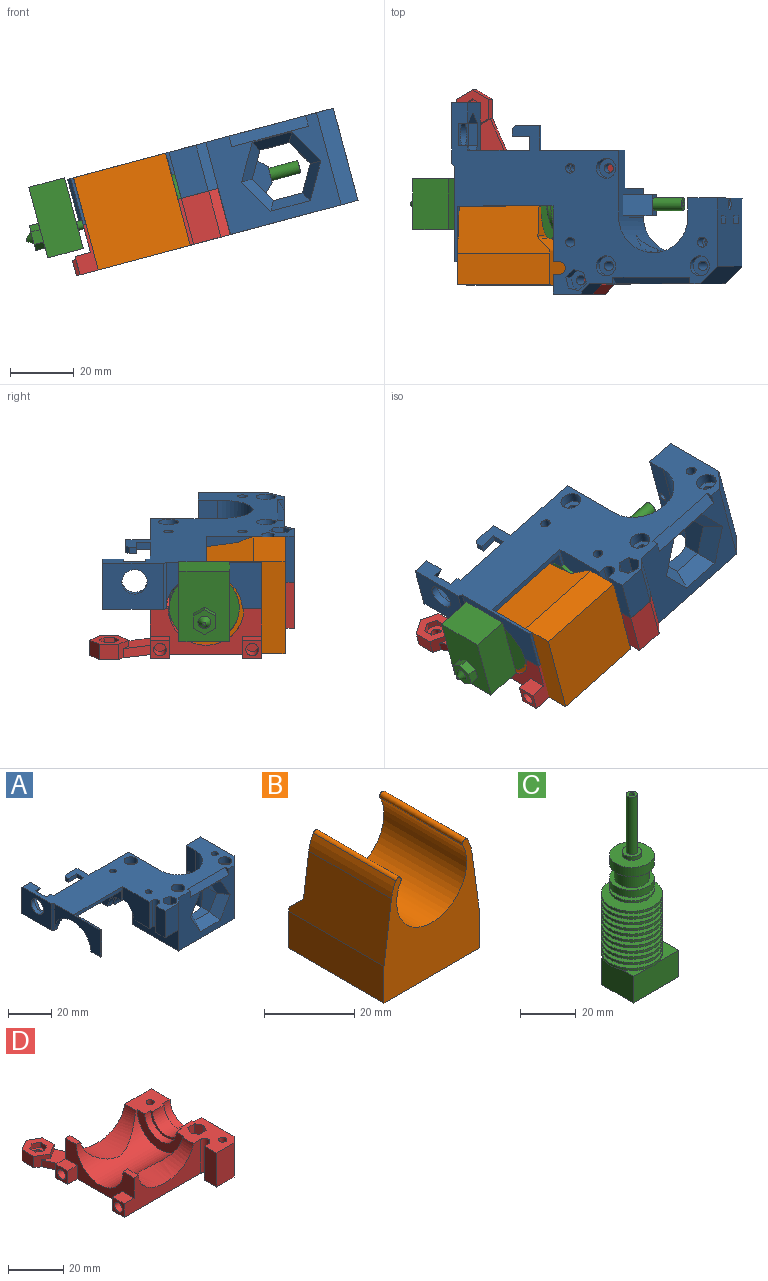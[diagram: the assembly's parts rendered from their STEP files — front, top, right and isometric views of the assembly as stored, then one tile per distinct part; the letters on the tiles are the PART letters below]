
ASSEMBLY  parts=4 mates=3
PART A: 169 faces, bbox 87.6x61.3x31.1 mm
  f0: plane 5.38x3mm, normal (-1,0,0), area 16.2mm2, adj f1,f165,f166,f168
  f1: plane 8.2x5.65mm, normal (0,1,0), area 34.3mm2, adj f0,f2,f5,f162,f163,f164,f165,f168
  f2: plane 8.9x3mm, normal (1,0,0), area 26.7mm2, adj f1,f3,f165,f168
  f3: plane 4x3mm, normal (0,1,0), area 12mm2, adj f2,f4,f165,f168
  f4: plane 3x2.63mm, normal (-1,0,0), area 7.9mm2, adj f3,f165,f166,f168
  f5: plane 8.2x2.5mm, normal (0,0,-1), area 20.5mm2, adj f1,f6,f162,f164
  f6: plane 8.2x5.65mm, normal (0,-1,0), area 34.3mm2, adj f5,f7,f159,f160,f161,f162,f163,f164
  f7: plane 5.6x3mm, normal (1,0,0), area 16.8mm2, adj f6,f8,f159,f161
  f8: plane 30x9.6mm, normal (0,1,0), area 264mm2, adj f7,f9,f20,f21,f22,f23,f155,f158
  f9: plane 5.6x4mm, normal (0,0,1), area 22.4mm2, adj f8,f10,f20,f22
  f10: plane 8.2x5.65mm, normal (0,-1,0), area 34.3mm2, adj f9,f11,f18,f19,f20,f21,f22,f164
  f11: plane 8.2x2.5mm, normal (0,0,1), area 20.5mm2, adj f10,f12,f18,f164
  f12: plane 8.2x5.65mm, normal (0,1,0), area 34.3mm2, adj f11,f13,f15,f16,f17,f18,f19,f164
  f13: plane 8.9x3mm, normal (-1,0,0), area 26.7mm2, adj f12,f14,f15,f17
  f14: plane 4x3mm, normal (0,1,0), area 12mm2, adj f13,f15,f16,f17
  f15: plane 8.9x4mm, normal (0,0,1), area 35.6mm2, adj f12,f13,f14,f16
  f16: plane 8.9x3mm, normal (1,0,0), area 26.7mm2, adj f12,f14,f15,f17
  f17: plane 8.9x4mm, normal (0,0,-1), area 35.6mm2, adj f12,f13,f14,f16
  f18: plane 5.65x2.5mm, normal (1,0,0), area 14.1mm2, adj f10,f11,f12,f19
  f19: plane 8.2x2.5mm, normal (0,0,-1), area 20.5mm2, adj f10,f12,f18,f164
  f20: plane 5.6x3mm, normal (1,0,0), area 16.8mm2, adj f8,f9,f10,f21
  f21: plane 5.6x4mm, normal (0,0,-1), area 22.4mm2, adj f8,f10,f20,f22
  f22: plane 5.6x3mm, normal (-1,0,0), area 16.8mm2, adj f8,f9,f10,f21
  f23: plane 86.5x60.2mm, normal (0,0,1), area 1918.9mm2, adj f8,f24,f94,f95,f96,f97,f99,f100
  f24: plane 25.08x15mm, normal (1,0,0), area 176.8mm2, adj f23,f25,f26,f91,f92,f93,f94,f139
  f25: plane 6.15x0.85mm, normal (0,0,-1), area 5.2mm2, adj f24,f93,f94,f95
  f26: plane 30.15x1.95mm, normal (0,-0.11,-0.99), area 59.2mm2, adj f24,f27,f91,f139
  f27: plane 13.14x12.5mm, normal (-1,0,0), area 70.2mm2, adj f26,f28,f70,f90,f91,f92,f139
  f28: cylinder r=8mm len=16mm, axis (-1,0,0), area 63.4mm2, adj f27,f29,f69,f70,f138,f139
  f29: plane 21.28x11.9mm, normal (0,0,-1), area 189.8mm2, adj f28,f30,f32,f34,f35,f36,f37,f38
  f30: cylinder r=1.5mm len=9mm, axis (0,0,1), area 84.8mm2, adj f29,f31
  f31: plane 6.69x6.69mm, normal (0,0,1), area 24.1mm2, adj f30,f140,f141,f142,f143,f144,f145
  f32: plane 4x3mm, normal (-0.87,0.5,0), area 13.9mm2, adj f29,f33,f34,f38
  f33: plane 6.93x6mm, normal (0,0,-1), area 24.1mm2, adj f32,f34,f35,f36,f37,f38,f153
  f34: plane 4x3.46mm, normal (0,1,0), area 13.9mm2, adj f29,f32,f33,f35
  f35: plane 4x3mm, normal (0.87,0.5,0), area 13.9mm2, adj f29,f33,f34,f36
  f36: plane 4x3mm, normal (0.87,-0.5,0), area 13.9mm2, adj f29,f33,f35,f37
  f37: plane 4x3.46mm, normal (0,-1,0), area 13.9mm2, adj f29,f33,f36,f38
  f38: plane 4x3mm, normal (-0.87,-0.5,0), area 13.9mm2, adj f29,f32,f33,f37
  f39: plane 30.1x23mm, normal (-1,0,0), area 451.3mm2, adj f29,f40,f54,f55,f56,f57,f58,f59
  f40: cylinder r=3.5mm len=4mm, axis (-1,0,0), area 22mm2, adj f39,f41,f54,f60
  f41: plane 13.2x7.4mm, normal (-1,0,0), area 59.1mm2, adj f40,f42,f46,f47,f53,f54,f55,f56
  f42: cylinder r=2mm len=4mm, axis (-1,0,0), area 18.8mm2, adj f41,f43,f45,f46,f53
  f43: cylinder r=3mm len=4mm, axis (0,0,1), area 9.9mm2, adj f42,f44,f45,f46,f53
  f44: bspline ~4.5x3.27mm, area 7.4mm2, adj f43,f46,f47,f53
  f45: cone r=2mm half-angle=45deg, axis (-1,0,0), area 0mm2, adj f42,f43
  f46: plane 4.03x3.55mm, normal (0,1,0), area 11.8mm2, adj f41,f42,f43,f44,f47
  f47: cylinder r=2mm len=13mm, axis (-1,0,0), area 142mm2, adj f41,f44,f46,f48,f53
  f48: plane 6.5x5mm, normal (1,0,0), area 19.9mm2, adj f47,f49,f50,f51,f52
  f49: plane 7.5x7.5mm, normal (0.71,0,0.71), area 68.9mm2, adj f48,f50,f52,f113
  f50: plane 20x7.5mm, normal (0,1,0), area 93.7mm2, adj f48,f49,f51,f113
  f51: plane 7.5x7.5mm, normal (0.71,0,-0.71), area 68.9mm2, adj f48,f50,f52,f113
  f52: plane 20x7.5mm, normal (0,-1,0), area 93.7mm2, adj f48,f49,f51,f113
  f53: plane 4.03x3.56mm, normal (0,-1,0), area 11.8mm2, adj f41,f42,f43,f44,f47
  f54: plane 4x0.4mm, normal (0,0,1), area 1.6mm2, adj f39,f40,f41,f55
  f55: cylinder r=3.5mm len=4mm, axis (1,0,0), area 22mm2, adj f39,f41,f54,f56
  f56: plane 6.2x4mm, normal (0,1,0), area 24.8mm2, adj f39,f41,f55,f57
  f57: cylinder r=3.5mm len=4mm, axis (-1,0,0), area 22mm2, adj f39,f41,f56,f58
  f58: plane 4x0.4mm, normal (0,0,-1), area 1.6mm2, adj f39,f41,f57,f59
  f59: cylinder r=3.5mm len=4mm, axis (1,0,0), area 22mm2, adj f39,f41,f58,f60
  f60: plane 6.2x4mm, normal (0,-1,0), area 24.8mm2, adj f39,f40,f41,f59
  f61: plane 22.5x9.5mm, normal (0,1,0), area 213.7mm2, adj f39,f62,f65,f113,f158
  f62: plane 12x9.5mm, normal (0,0,-1), area 106.9mm2, adj f61,f63,f65,f112,f113
  f63: cylinder r=1.5mm len=4mm, axis (0,0,1), area 37.7mm2, adj f62,f64
  f64: plane 6.3x6.3mm, normal (0,0,1), area 24.1mm2, adj f63,f146
  f65: plane 12x7.5mm, normal (1,0,0), area 76.5mm2, adj f61,f62,f66,f70,f112
  f66: cylinder r=8mm len=16mm, axis (-1,0,0), area 100.5mm2, adj f29,f39,f65,f67,f70
  f67: plane 16x8mm, normal (1,0,0), area 23.6mm2, adj f29,f66,f68,f70
  f68: cylinder r=7mm len=14mm, axis (-1,0,0), area 129.7mm2, adj f29,f67,f69,f70
  f69: plane 16x8mm, normal (-1,0,0), area 23.6mm2, adj f28,f29,f68,f70
  f70: plane 13.65x9.93mm, normal (0,0,-1), area 117.7mm2, adj f27,f28,f65,f66,f67,f68,f69,f71
  f71: extruded ~28x11mm, area 304.7mm2, adj f70,f72,f73,f74,f77,f90,f92,f93
  f72: plane 20x5.25mm, normal (0,0,-1), area 94.5mm2, adj f71,f73,f93,f96,f97,f99,f100
  f73: plane 5.66x2mm, normal (0,-1,0), area 7.7mm2, adj f71,f72,f74,f100
  f74: plane 7.16x6.21mm, normal (0,0.87,0.5), area 27.3mm2, adj f71,f73,f75,f100,f102,f103
  f75: plane 6.93x3mm, normal (0,0,1), area 20.8mm2, adj f74,f76,f100,f102
  f76: plane 6x3.46mm, normal (0,-0.87,0.5), area 20.8mm2, adj f75,f100,f101,f102
  f77: plane 1.34x0.77mm, normal (-1,0,0), area 0.5mm2, adj f71,f103,f112
  f78: cylinder r=1.5mm len=3mm, axis (0,0,-1), area 25.9mm2, adj f70,f79
  f79: plane 8.5x5.6mm, normal (0,0,1), area 40.5mm2, adj f78,f80,f88,f89,f112
  f80: plane 8.5x2.5mm, normal (-1,0,0), area 21.3mm2, adj f79,f81,f88,f112
  f81: plane 8.5x5.6mm, normal (0,0,-1), area 40.5mm2, adj f80,f82,f88,f89,f112
  f82: cylinder r=1.5mm len=3.6mm, axis (0,0,-1), area 33.9mm2, adj f81,f83
  f83: plane 8.5x5.6mm, normal (0,0,1), area 40.5mm2, adj f82,f84,f86,f87,f112
  f84: plane 8.5x2.5mm, normal (-1,0,0), area 21.2mm2, adj f83,f85,f86,f112
  f85: plane 8.5x5.6mm, normal (0,0,-1), area 40.5mm2, adj f84,f86,f87,f112,f154
  f86: plane 5.6x2.5mm, normal (0,1,0), area 14mm2, adj f83,f84,f85,f87
  f87: plane 8.5x2.5mm, normal (1,0,0), area 21.2mm2, adj f83,f85,f86,f112
  f88: plane 5.6x2.5mm, normal (0,1,0), area 14mm2, adj f79,f80,f81,f89
  f89: plane 8.5x2.5mm, normal (1,0,0), area 21.3mm2, adj f79,f81,f88,f112
  f90: extruded ~9.48x7.66mm, area 36mm2, adj f27,f70,f71,f92
  f91: cylinder r=13mm len=30.15mm, axis (-1,0,0), area 163.6mm2, adj f24,f26,f27,f92
  f92: cylinder r=1mm len=30.15mm, axis (-1,0,0), area 48.1mm2, adj f24,f27,f71,f90,f91,f93
  f93: extruded ~23.85x11.25mm, area 74.4mm2, adj f24,f25,f71,f72,f92,f95
  f94: plane 15x0.85mm, normal (0,-1,0), area 12.8mm2, adj f23,f24,f25,f95
  f95: plane 30x15mm, normal (-1,0,0), area 239.3mm2, adj f23,f25,f93,f94,f96
  f96: plane 15x1mm, normal (-0.71,-0.71,0), area 21.2mm2, adj f23,f72,f95,f97
  f97: plane 19x15mm, normal (-1,0,0), area 234.7mm2, adj f23,f72,f96,f98,f99
  f98: cylinder r=4mm len=8mm, axis (-1,0,0), area 56.5mm2, adj f97,f102
  f99: plane 15x5.25mm, normal (0,1,0), area 78.7mm2, adj f23,f72,f97,f100
  f100: plane 15x15mm, normal (1,0,0), area 104.7mm2, adj f23,f72,f73,f74,f75,f76,f99,f101
  f101: plane 6x3.46mm, normal (0,-0.87,-0.5), area 20.8mm2, adj f23,f76,f100,f102
  f102: plane 13.86x12mm, normal (1,0,0), area 74.4mm2, adj f23,f74,f75,f76,f98,f101,f103
  f103: plane 15.57x6.57mm, normal (0,0.87,-0.5), area 54.4mm2, adj f23,f71,f74,f77,f102,f104,f112
  f104: plane 2.66x1.54mm, normal (1,0,0), area 2mm2, adj f23,f103,f112
  f105: plane 4.5x2.1mm, normal (-1,0,0), area 9.4mm2, adj f23,f106,f107,f112
  f106: plane 8.7x7.75mm, normal (0,0,-1), area 42.4mm2, adj f105,f107,f108,f109,f110,f111,f112
  f107: plane 5.45x2.1mm, normal (0,-1,0), area 11.4mm2, adj f23,f105,f106,f108
  f108: plane 2.25x2.1mm, normal (-1,0,0), area 4.7mm2, adj f23,f106,f107,f109
  f109: plane 2.1x1mm, normal (-0.71,0.71,0), area 3mm2, adj f23,f106,f108,f110
  f110: plane 7.7x2.1mm, normal (0,1,0), area 16.2mm2, adj f23,f106,f109,f111
  f111: plane 7.75x2.1mm, normal (1,0,0), area 16.3mm2, adj f23,f106,f110,f112
  f112: plane 49.15x15mm, normal (0,1,0), area 362.1mm2, adj f23,f62,f65,f70,f71,f77,f79,f80
  f113: plane 30x21mm, normal (1,0,0), area 230mm2, adj f23,f49,f50,f51,f52,f61,f62,f112
  f114: cylinder r=11.25mm len=30mm, axis (0,0,1), area 795.5mm2, adj f23,f113,f115,f122,f123,f124,f125,f126
  f115: plane 10.99x9.27mm, normal (0.87,0,-0.5), area 69.8mm2, adj f114,f116,f122,f126
  f116: plane 11.2x8.2mm, normal (0.75,-0.5,-0.43), area 67.2mm2, adj f115,f117,f121,f131
  f117: plane 11.2x8.2mm, normal (0.75,-0.5,0.43), area 67.2mm2, adj f116,f118,f122,f131
  f118: plane 12.93x5.2mm, normal (0,-0.5,0.87), area 67.2mm2, adj f117,f119,f123,f131
  f119: plane 11.2x8.2mm, normal (-0.75,-0.5,0.43), area 67.2mm2, adj f118,f120,f124,f131
  f120: plane 11.2x8.2mm, normal (-0.75,-0.5,-0.43), area 67.2mm2, adj f119,f121,f125,f131
  f121: plane 12.93x5.2mm, normal (0,-0.5,-0.87), area 67.2mm2, adj f116,f120,f126,f131
  f122: plane 10.99x9.27mm, normal (0.87,0,0.5), area 69.8mm2, adj f114,f115,f117,f123
  f123: plane 9.47x5.65mm, normal (0,0,1), area 46.4mm2, adj f114,f118,f122,f124
  f124: plane 10.52x9.18mm, normal (-0.87,0,0.5), area 67.8mm2, adj f114,f119,f123,f125
  f125: plane 10.52x9.18mm, normal (-0.87,0,-0.5), area 67.8mm2, adj f114,f120,f124,f126
  f126: plane 9.47x5.65mm, normal (0,0,-1), area 46.4mm2, adj f114,f115,f121,f125
  f127: plane 30x5.5mm, normal (0.71,-0.71,0), area 233.3mm2, adj f23,f131,f158,f164
  f128: plane 3.46x2mm, normal (-1,0,0), area 3.5mm2, adj f23,f129,f131
  f129: plane 25x3.46mm, normal (0,-0.87,0.5), area 100mm2, adj f23,f128,f130,f131
  f130: plane 3.46x2mm, normal (1,0,0), area 3.5mm2, adj f23,f129,f131
  f131: plane 36x30mm, normal (0,-1,0), area 558.9mm2, adj f23,f116,f117,f118,f119,f120,f121,f127
  f132: plane 30x3.2mm, normal (0.71,-0.71,0), area 70mm2, adj f23,f29,f39,f131,f133,f158
  f133: plane 15x8.8mm, normal (0,-1,0), area 132mm2, adj f23,f29,f132,f134
  f134: plane 15x6.2mm, normal (-1,0,0), area 93mm2, adj f23,f29,f133,f135
  f135: plane 15x2mm, normal (0,1,0), area 30mm2, adj f23,f29,f134,f136
  f136: cylinder r=2mm len=15mm, axis (0,0,1), area 94.2mm2, adj f23,f29,f135,f137
  f137: plane 15x2mm, normal (0,-1,0), area 30mm2, adj f23,f29,f136,f138
  f138: plane 17.5x15mm, normal (-1,0,0), area 216.8mm2, adj f23,f28,f29,f137,f139
  f139: plane 31.15x7.02mm, normal (0,-1,0), area 63.3mm2, adj f23,f24,f26,f27,f28,f138
  f140: plane 6x3.35mm, normal (0.26,0.97,0), area 20.8mm2, adj f23,f31,f141,f145
  f141: plane 6x2.45mm, normal (-0.71,0.71,0), area 20.8mm2, adj f23,f31,f140,f142
  f142: plane 6x3.35mm, normal (-0.97,-0.26,0), area 20.8mm2, adj f23,f31,f141,f143
  f143: plane 6x3.35mm, normal (-0.26,-0.97,0), area 20.8mm2, adj f23,f31,f142,f144
  f144: plane 6x2.45mm, normal (0.71,-0.71,0), area 20.8mm2, adj f23,f31,f143,f145
  f145: plane 6x3.35mm, normal (0.97,0.26,0), area 20.8mm2, adj f23,f31,f140,f144
  f146: cylinder r=3.15mm len=6.3mm, axis (0,0,1), area 69.3mm2, adj f23,f64
  f147: cylinder r=3.15mm len=6.3mm, axis (0,0,1), area 69.3mm2, adj f23,f148
  f148: plane 6.3x6.3mm, normal (0,0,1), area 24.1mm2, adj f147,f149
  f149: cylinder r=1.5mm len=26.5mm, axis (0,0,1), area 249.8mm2, adj f148,f158
  f150: cylinder r=3.15mm len=6.3mm, axis (0,0,1), area 69.3mm2, adj f23,f151
  f151: plane 6.3x6.3mm, normal (0,0,1), area 24.1mm2, adj f150,f152
  f152: cylinder r=1.5mm len=26.5mm, axis (0,0,1), area 249.8mm2, adj f151,f158
  f153: cylinder r=1.5mm len=11mm, axis (0,0,-1), area 103.7mm2, adj f23,f33
  f154: cylinder r=1.5mm len=3.65mm, axis (0,0,-1), area 34.4mm2, adj f23,f85
  f155: plane 30x6mm, normal (-1,0,0), area 175.1mm2, adj f8,f23,f114,f156,f158
  f156: cylinder r=1.25mm len=9.1mm, axis (1,0,0), area 71.5mm2, adj f155,f157
  f157: cone r=1.25mm half-angle=45deg, axis (1,0,0), area 6.7mm2, adj f156,f164
  f158: plane 41.6x30.1mm, normal (0,0,-1), area 788.6mm2, adj f8,f39,f61,f113,f114,f127,f131,f132
  f159: plane 5.6x4mm, normal (0,0,1), area 22.4mm2, adj f6,f7,f8,f160
  f160: plane 5.6x3mm, normal (-1,0,0), area 16.8mm2, adj f6,f8,f159,f161
  f161: plane 5.6x4mm, normal (0,0,-1), area 22.4mm2, adj f6,f7,f8,f160
  f162: plane 5.65x2.5mm, normal (1,0,0), area 14.1mm2, adj f1,f5,f6,f163
  f163: plane 8.2x2.5mm, normal (0,0,1), area 20.5mm2, adj f1,f6,f162,f164
  f164: plane 30x21.5mm, normal (1,0,0), area 607.1mm2, adj f1,f5,f6,f8,f10,f11,f12,f19
  f165: plane 8.9x4mm, normal (0,0,-1), area 28.1mm2, adj f0,f1,f2,f3,f4,f166
  f166: cylinder r=1.55mm len=15mm, axis (0,0,1), area 119.6mm2, adj f0,f4,f23,f165,f167,f168
  f167: plane 3.1x3.1mm, normal (0,0,1), area 7.5mm2, adj f166
  f168: plane 8.9x4mm, normal (0,0,1), area 28.1mm2, adj f0,f1,f2,f3,f4,f166
PART B: 18 faces, bbox 30x30x31.8 mm
  f0: plane 16.41x9.64mm, normal (0,1,0), area 54.9mm2, adj f1,f2,f3,f4,f16
  f1: cylinder r=11mm len=26.6mm, axis (0,1,0), area 1179.5mm2, adj f0,f2,f10,f11,f12,f14,f15,f16
  f2: cylinder r=0.88mm len=26mm, axis (0,1,0), area 71.5mm2, adj f0,f1,f3,f11
  f3: cylinder r=12.75mm len=26mm, axis (0,1,0), area 115.6mm2, adj f0,f2,f4,f11
  f4: plane 30.01x17.15mm, normal (-0.99,0,0.14), area 462.1mm2, adj f0,f3,f5,f11,f13,f14,f16,f17
  f5: plane 30x10mm, normal (-1,0,0), area 300mm2, adj f4,f6,f11,f13
  f6: plane 30x30mm, normal (0,0,-1), area 900mm2, adj f5,f7,f11,f13
  f7: plane 30x10mm, normal (1,0,0), area 300mm2, adj f6,f8,f11,f13
  f8: plane 30.01x17.15mm, normal (0.99,0,0.14), area 462.1mm2, adj f7,f9,f11,f12,f13,f14,f15,f17
  f9: cylinder r=12.75mm len=26mm, axis (0,1,0), area 115.6mm2, adj f8,f10,f11,f12
  f10: cylinder r=0.88mm len=26mm, axis (0,1,0), area 71.5mm2, adj f1,f9,f11,f12
  f11: plane 31.82x30mm, normal (0,-1,0), area 561.9mm2, adj f1,f2,f3,f4,f5,f6,f7,f8
  f12: plane 16.41x9.64mm, normal (0,1,0), area 54.9mm2, adj f1,f8,f9,f10,f15
  f13: plane 30x10.59mm, normal (0,1,0), area 317.5mm2, adj f4,f5,f6,f7,f8,f17
  f14: plane 29.64x3.41mm, normal (0,0.71,0.71), area 139.3mm2, adj f1,f4,f8,f15,f16,f17
  f15: cylinder r=1mm len=11.77mm, axis (1,0,0), area 8.4mm2, adj f1,f8,f12,f14
  f16: cylinder r=1mm len=11.77mm, axis (1,0,0), area 8.4mm2, adj f0,f1,f4,f14
  f17: cylinder r=1mm len=29.84mm, axis (-1,0,0), area 23.4mm2, adj f4,f8,f13,f14
PART C: 77 faces, bbox 26.8x22x88.9 mm
  f0: plane 1x1mm, normal (0,0,-1), area 0.8mm2, adj f1
  f1: cone r=0.5mm half-angle=36.9deg, axis (0,0,1), area 19.6mm2, adj f0,f8
  f2: plane 4.04x3mm, normal (0,-1,0), area 12.1mm2, adj f3,f7,f8,f9
  f3: plane 3.5x3mm, normal (0.87,-0.5,0), area 12.1mm2, adj f2,f4,f8,f9
  f4: plane 3.5x3mm, normal (0.87,0.5,0), area 12.1mm2, adj f3,f5,f8,f9
  f5: plane 4.04x3mm, normal (0,1,0), area 12.1mm2, adj f4,f6,f8,f9
  f6: plane 3.5x3mm, normal (-0.87,0.5,0), area 12.1mm2, adj f5,f7,f8,f9
  f7: plane 3.5x3mm, normal (-0.87,-0.5,0), area 12.1mm2, adj f2,f6,f8,f9
  f8: plane 8.08x7mm, normal (0,0,-1), area 29.9mm2, adj f1,f2,f3,f4,f5,f6,f7
  f9: plane 23x16mm, normal (0,0,-1), area 325.6mm2, adj f2,f3,f4,f5,f6,f7,f10,f11
  f10: plane 23x11.6mm, normal (0,-1,0), area 266.8mm2, adj f9,f11,f13,f14
  f11: plane 16x11.6mm, normal (1,0,0), area 185.6mm2, adj f9,f10,f12,f14
  f12: plane 23x11.6mm, normal (0,1,0), area 266.8mm2, adj f9,f11,f13,f14
  f13: plane 16x11.6mm, normal (-1,0,0), area 185.6mm2, adj f9,f10,f12,f14
  f14: plane 23x16mm, normal (0,0,1), area 362.1mm2, adj f10,f11,f12,f13,f15
  f15: cylinder r=1.38mm len=2.75mm, axis (0,0,-1), area 23.8mm2, adj f14,f16
  f16: plane 22x22mm, normal (0,0,-1), area 374.2mm2, adj f15,f17
  f17: cylinder r=11mm len=22mm, axis (0,0,-1), area 69.1mm2, adj f16,f18
  f18: plane 22x22mm, normal (0,0,1), area 267mm2, adj f17,f19
  f19: cone r=6mm half-angle=4deg, axis (0,0,-1), area 56.2mm2, adj f18,f20
  f20: plane 22x22mm, normal (0,0,-1), area 270.9mm2, adj f19,f21
  f21: cylinder r=11mm len=22mm, axis (0,0,-1), area 69.1mm2, adj f20,f22
  f22: plane 22x22mm, normal (0,0,1), area 273.5mm2, adj f21,f23
  f23: cone r=5.83mm half-angle=4deg, axis (0,0,-1), area 54.6mm2, adj f22,f24
  f24: plane 22x22mm, normal (0,0,-1), area 277.2mm2, adj f23,f25
  f25: cylinder r=11mm len=22mm, axis (0,0,-1), area 69.1mm2, adj f24,f26
  f26: plane 22x22mm, normal (0,0,1), area 279.7mm2, adj f25,f27
  f27: cone r=5.65mm half-angle=4deg, axis (0,0,-1), area 52.9mm2, adj f26,f28
  f28: plane 22x22mm, normal (0,0,-1), area 283.3mm2, adj f27,f29
  f29: cylinder r=11mm len=22mm, axis (0,0,-1), area 69.1mm2, adj f28,f30
  f30: plane 22x22mm, normal (0,0,1), area 285.7mm2, adj f29,f31
  f31: cone r=5.48mm half-angle=4deg, axis (0,0,-1), area 51.3mm2, adj f30,f32
  f32: plane 22x22mm, normal (0,0,-1), area 289.3mm2, adj f31,f33
  f33: cylinder r=11mm len=22mm, axis (0,0,-1), area 69.1mm2, adj f32,f34
  f34: plane 22x22mm, normal (0,0,1), area 291.6mm2, adj f33,f35
  f35: cone r=5.31mm half-angle=4deg, axis (0,0,-1), area 49.7mm2, adj f34,f36
  f36: plane 22x22mm, normal (0,0,-1), area 295mm2, adj f35,f37
  f37: cylinder r=11mm len=22mm, axis (0,0,-1), area 69.1mm2, adj f36,f38
  f38: plane 22x22mm, normal (0,0,1), area 297.3mm2, adj f37,f39
  f39: cone r=5.14mm half-angle=4deg, axis (0,0,-1), area 48mm2, adj f38,f40
  f40: plane 22x22mm, normal (0,0,-1), area 300.6mm2, adj f39,f41
  f41: cylinder r=11mm len=22mm, axis (0,0,-1), area 69.1mm2, adj f40,f42
  f42: plane 22x22mm, normal (0,0,1), area 302.8mm2, adj f41,f43
  f43: cone r=4.96mm half-angle=4deg, axis (0,0,-1), area 46.4mm2, adj f42,f44
  f44: plane 22x22mm, normal (0,0,-1), area 306mm2, adj f43,f45
  f45: cylinder r=11mm len=22mm, axis (0,0,-1), area 69.1mm2, adj f44,f46
  f46: plane 22x22mm, normal (0,0,1), area 308.1mm2, adj f45,f47
  f47: cone r=4.79mm half-angle=4deg, axis (0,0,-1), area 44.8mm2, adj f46,f48
  f48: plane 22x22mm, normal (0,0,-1), area 311.2mm2, adj f47,f49
  f49: cylinder r=11mm len=22mm, axis (0,0,-1), area 69.1mm2, adj f48,f50
  f50: plane 22x22mm, normal (0,0,1), area 313.2mm2, adj f49,f51
  f51: cone r=4.62mm half-angle=4deg, axis (0,0,-1), area 43.1mm2, adj f50,f52
  f52: plane 22x22mm, normal (0,0,-1), area 316.1mm2, adj f51,f53
  f53: cylinder r=11mm len=22mm, axis (0,0,-1), area 69.1mm2, adj f52,f54
  f54: plane 22x22mm, normal (0,0,1), area 318.1mm2, adj f53,f55
  f55: cone r=4.44mm half-angle=4deg, axis (0,0,-1), area 41.5mm2, adj f54,f56
  f56: plane 22x22mm, normal (0,0,-1), area 321mm2, adj f55,f57
  f57: cylinder r=11mm len=22mm, axis (0,0,-1), area 69.1mm2, adj f56,f58
  f58: plane 22x22mm, normal (0,0,1), area 322.8mm2, adj f57,f59
  f59: cone r=4.27mm half-angle=4deg, axis (0,0,-1), area 39.9mm2, adj f58,f60
  f60: plane 16x16mm, normal (0,0,-1), area 146.5mm2, adj f59,f61
  f61: cylinder r=8mm len=16mm, axis (0,0,-1), area 50.3mm2, adj f60,f62
  f62: plane 16x16mm, normal (0,0,1), area 148.3mm2, adj f61,f63
  f63: cone r=4.1mm half-angle=4deg, axis (0,0,-1), area 38.2mm2, adj f62,f64
  f64: plane 16x16mm, normal (0,0,-1), area 150.9mm2, adj f63,f65
  f65: cylinder r=8mm len=16mm, axis (0,0,-1), area 150.8mm2, adj f64,f66
  f66: plane 16x16mm, normal (0,0,1), area 78.3mm2, adj f65,f67
  f67: cylinder r=6.25mm len=12.5mm, axis (0,0,-1), area 235.6mm2, adj f66,f68
  f68: plane 16x16mm, normal (0,0,-1), area 78.3mm2, adj f67,f69
  f69: cylinder r=8mm len=16mm, axis (0,0,-1), area 201.1mm2, adj f68,f70
  f70: plane 16x16mm, normal (0,0,1), area 162.6mm2, adj f69,f71
  f71: cylinder r=3.5mm len=7mm, axis (0,0,-1), area 33mm2, adj f70,f72
  f72: plane 7x7mm, normal (0,0,1), area 25.9mm2, adj f71,f74
  f73: cylinder r=1mm len=25mm, axis (0,0,-1), area 157.1mm2, adj f75,f76
  f74: cylinder r=2mm len=25mm, axis (0,0,-1), area 314.2mm2, adj f72,f75
  f75: plane 4x4mm, normal (0,0,1), area 9.4mm2, adj f73,f74
  f76: plane 2x2mm, normal (0,0,1), area 3.1mm2, adj f73
PART D: 65 faces, bbox 50.1x64.3x15 mm
  f0: plane 35x15mm, normal (-1,0,0), area 229.6mm2, adj f3,f4,f5,f6,f7,f52,f55,f56
  f1: plane 13.65x10.5mm, normal (0,0,1), area 125.6mm2, adj f3,f8,f11,f36,f37,f38,f39,f40
  f2: plane 20.7x13.65mm, normal (0,0,1), area 197mm2, adj f7,f9,f10,f11,f12,f13,f14,f33
  f3: plane 48.9x15mm, normal (0,1,0), area 441.6mm2, adj f0,f1,f4,f6,f11,f15,f16,f23
  f4: plane 5.58x2.25mm, normal (0,0,1), area 12.5mm2, adj f0,f3,f52,f53
  f5: plane 5.58x2.25mm, normal (0,0,1), area 12.5mm2, adj f0,f7,f52,f54
  f6: plane 64.29x50.08mm, normal (0,0,-1), area 1796.7mm2, adj f0,f3,f7,f10,f11,f12,f13,f14
  f7: plane 39x15mm, normal (0,-1,0), area 319.4mm2, adj f0,f2,f5,f6,f14,f54,f62,f63
  f8: cylinder r=1.5mm len=11.5mm, axis (0,0,1), area 108.4mm2, adj f1,f41
  f9: cylinder r=1.5mm len=11.5mm, axis (0,0,1), area 108.4mm2, adj f2,f34
  f10: plane 15x6.2mm, normal (-1,0,0), area 93mm2, adj f2,f6,f12,f13
  f11: plane 42.2x15mm, normal (1,0,0), area 532.5mm2, adj f1,f2,f3,f6,f33,f37
  f12: plane 15x8.9mm, normal (0,-1,0), area 133.5mm2, adj f2,f6,f10,f33
  f13: plane 15x2mm, normal (0,1,0), area 30mm2, adj f2,f6,f10,f14
  f14: cylinder r=2mm len=15mm, axis (0,0,1), area 94.2mm2, adj f2,f6,f7,f13
  f15: plane 8.63x3.95mm, normal (-0.91,-0.42,0), area 28.5mm2, adj f3,f6,f21,f23
  f16: plane 10x4.58mm, normal (0.91,0.42,0), area 33mm2, adj f3,f6,f17,f23
  f17: plane 6.06x5mm, normal (1,0,0), area 30.3mm2, adj f6,f16,f18,f22,f24
  f18: plane 5.25x5mm, normal (0.5,0.87,0), area 30.3mm2, adj f6,f17,f19,f24
  f19: plane 5.25x5mm, normal (-0.5,0.87,0), area 30.3mm2, adj f6,f18,f20,f24
  f20: plane 6.06x5mm, normal (-1,0,0), area 30.3mm2, adj f6,f19,f21,f24
  f21: plane 5.25x5mm, normal (-0.5,-0.87,0), area 20.4mm2, adj f6,f15,f20,f22,f23,f24
  f22: plane 5.25x3.03mm, normal (0.5,-0.87,0), area 12.1mm2, adj f17,f21,f23,f24
  f23: plane 12.7x10mm, normal (0,0,1), area 72.8mm2, adj f3,f15,f16,f21,f22
  f24: plane 12.12x10.5mm, normal (0,0,1), area 69.3mm2, adj f17,f18,f19,f20,f21,f22,f25,f26
  f25: plane 3.18x2.25mm, normal (1,0,0), area 7.1mm2, adj f24,f26,f30,f31
  f26: plane 2.75x2.25mm, normal (0.5,0.87,0), area 7.1mm2, adj f24,f25,f27,f31
  f27: plane 2.75x2.25mm, normal (-0.5,0.87,0), area 7.1mm2, adj f24,f26,f28,f31
  f28: plane 3.18x2.25mm, normal (-1,0,0), area 7.1mm2, adj f24,f27,f29,f31
  f29: plane 2.75x2.25mm, normal (-0.5,-0.87,0), area 7.1mm2, adj f24,f28,f30,f31
  f30: plane 2.75x2.25mm, normal (0.5,-0.87,0), area 7.1mm2, adj f24,f25,f29,f31
  f31: plane 6.35x5.5mm, normal (0,0,1), area 19.1mm2, adj f25,f26,f27,f28,f29,f30,f32
  f32: cylinder r=1.5mm len=3mm, axis (0,0,1), area 25.9mm2, adj f6,f31
  f33: plane 15x3mm, normal (0.71,-0.71,0), area 63.6mm2, adj f2,f6,f11,f12
  f34: plane 6x6mm, normal (0,0,-1), area 21.2mm2, adj f9,f35
  f35: cylinder r=3mm len=6mm, axis (0,0,-1), area 66mm2, adj f6,f34
  f36: plane 16x8mm, normal (1,0,0), area 23.6mm2, adj f1,f2,f37,f38
  f37: cylinder r=8mm len=16mm, axis (1,0,0), area 100.5mm2, adj f1,f2,f11,f36
  f38: cylinder r=7mm len=14mm, axis (-1,0,0), area 129.7mm2, adj f1,f2,f36,f39
  f39: plane 16x8mm, normal (-1,0,0), area 23.6mm2, adj f1,f2,f38,f40
  f40: cylinder r=8mm len=16mm, axis (-1,0,0), area 75.4mm2, adj f1,f2,f39,f51
  f41: plane 6x6mm, normal (0,0,-1), area 21.2mm2, adj f8,f42
  f42: cylinder r=3mm len=6mm, axis (0,0,-1), area 66mm2, adj f6,f41
  f43: plane 13.2x3.46mm, normal (0,1,0), area 45.7mm2, adj f2,f44,f48,f49
  f44: plane 13.2x3mm, normal (-0.87,0.5,0), area 45.7mm2, adj f2,f43,f45,f49
  f45: plane 13.2x3mm, normal (-0.87,-0.5,0), area 45.7mm2, adj f2,f44,f46,f49
  f46: plane 13.2x3.46mm, normal (0,-1,0), area 45.7mm2, adj f2,f45,f47,f49
  f47: plane 13.2x3mm, normal (0.87,-0.5,0), area 45.7mm2, adj f2,f46,f48,f49
  f48: plane 13.2x3mm, normal (0.87,0.5,0), area 45.7mm2, adj f2,f43,f47,f49
  f49: plane 6.93x6mm, normal (0,0,1), area 24.1mm2, adj f43,f44,f45,f46,f47,f48,f50
  f50: cylinder r=1.5mm len=3mm, axis (0,0,1), area 17mm2, adj f6,f49
  f51: plane 23.85x11.93mm, normal (-1,0,0), area 122.8mm2, adj f1,f2,f40,f52
  f52: cylinder r=11.93mm len=31mm, axis (-1,0,0), area 660.7mm2, adj f0,f1,f2,f4,f5,f51,f53,f54
  f53: extruded ~28x11.36mm, area 319.1mm2, adj f1,f3,f4,f52
  f54: extruded ~28x11.36mm, area 319.1mm2, adj f2,f5,f7,f52
  f55: plane 6x5mm, normal (0,-1,0), area 30mm2, adj f0,f6,f56,f58
  f56: plane 6x5mm, normal (0,0,1), area 30mm2, adj f0,f3,f55,f58
  f57: cylinder r=2mm len=5mm, axis (1,0,0), area 62.8mm2, adj f58,f59
  f58: plane 6x6mm, normal (-1,0,0), area 23.4mm2, adj f3,f6,f55,f56,f57
  f59: plane 4x4mm, normal (-1,0,0), area 12.6mm2, adj f57
  f60: plane 6x5mm, normal (0,1,0), area 30mm2, adj f0,f6,f62,f63
  f61: cylinder r=2mm len=5mm, axis (1,0,0), area 62.8mm2, adj f63,f64
  f62: plane 6x5mm, normal (0,0,1), area 30mm2, adj f0,f7,f60,f63
  f63: plane 6x6mm, normal (-1,0,0), area 23.4mm2, adj f6,f7,f60,f61,f62
  f64: plane 4x4mm, normal (-1,0,0), area 12.6mm2, adj f61
PLACE A rot(axis=(0,-1,0),15deg) t=(99.68,-31.16,-84.81)mm
PLACE B rot(axis=(-0.48,-0.62,-0.62),129deg) t=(80.49,-31.49,-74.42)mm
PLACE C rot(axis=(0.61,0,0.79),180deg) t=(36.68,-6.09,-86.16)mm
PLACE D rot(axis=(0,-1,0),15deg) t=(73.26,-11.76,-91.89)mm
MATE fastened B.f1 <-> C.f17  axis (0.97,0,0.26) through (80.49,-6.09,-74.42)mm
MATE fastened D.f9 <-> A.f30  axis (-0.26,0,0.97) through (92.65,-30.02,-71.16)mm
MATE fastened C.f17 <-> A.f28  axis (0.97,0,0.26) through (96.91,-6.09,-70.02)mm
